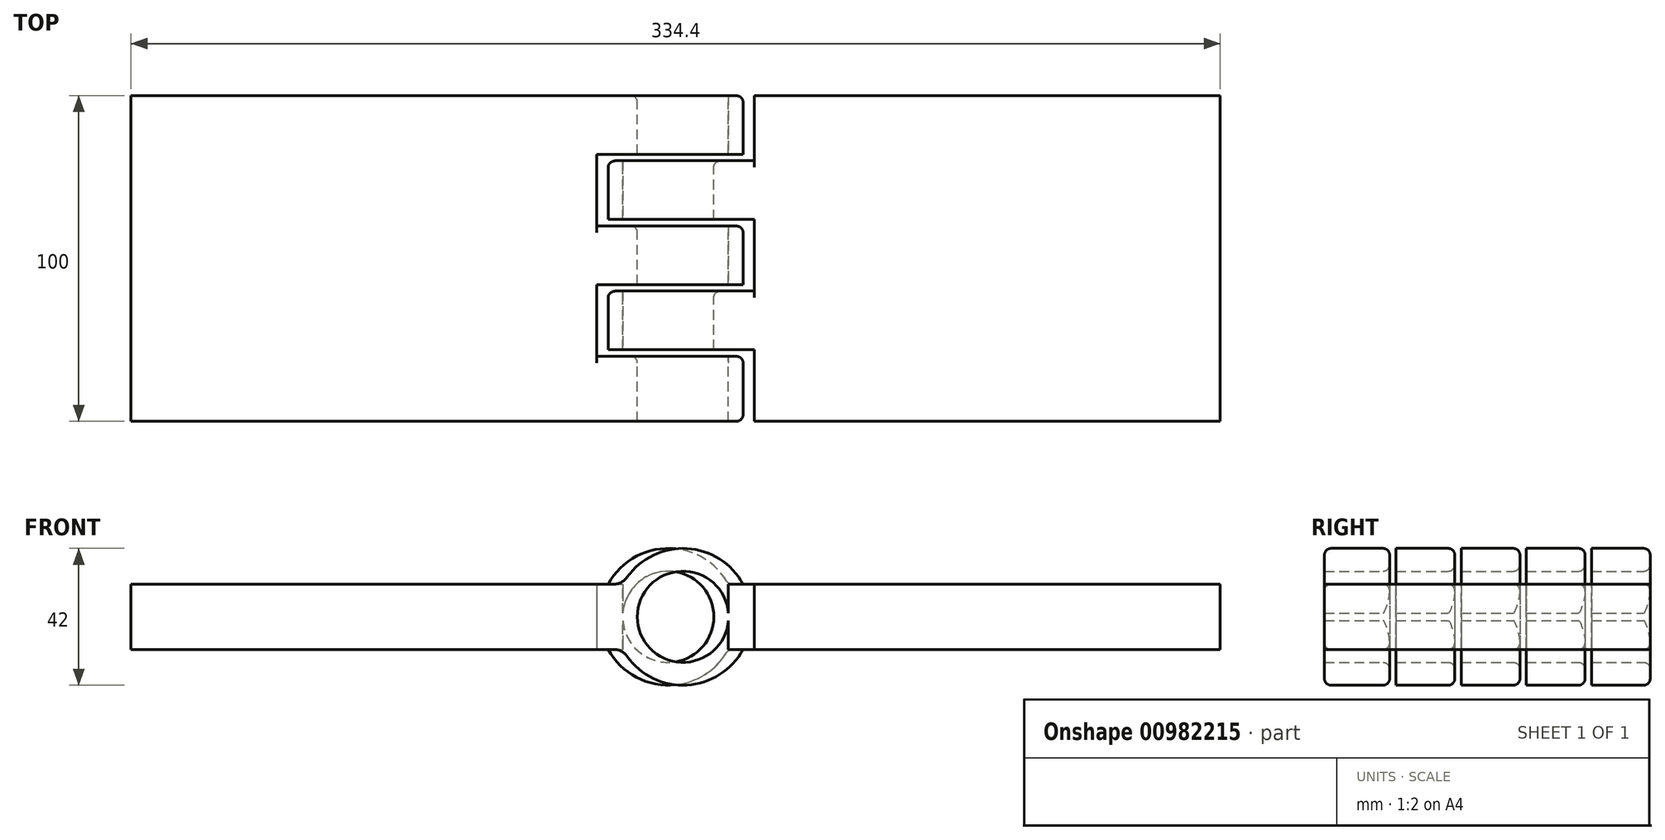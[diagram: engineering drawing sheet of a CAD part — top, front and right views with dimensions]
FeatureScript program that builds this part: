
annotation { "Feature Type Name" : "Feature", "Feature Type Description" : "" }
export const myFeature = defineFeature(function(context is Context, id is Id, definition is map)
    precondition{}
    {
        {
            var Q0;
            Q0=qCreatedBy(makeId("Front.planeOp"),FACE);
            var sketch = newSketch(context, id + "F0", { "sketchPlane" : qUnion([Q0])});
            skPoint(sketch, "E0.middle", {"position": v(0, 0) * mm});
            skPoint(sketch, "E0.left.start.orphan", {"position": v(100.03, 12.5) * mm});
            skPoint(sketch, "E1.orphan", {"position": v(100.2, -10) * mm});
            skArc(sketch, "E2", {"start": v(58.29, -10) * mm, "mid": v(97.76, 0) * mm, "end": v(58.29, 10) * mm});
            skCircle(sketch, "E3", {"center": v(76.76, 0) * mm, "radius": 10 * mm});
            skLineSegment(sketch, "E4", {"start": v(-92.7, 10) * mm, "end": v(77.7, 10) * mm});
            skLineSegment(sketch, "E5", {"start": v(-92.7, -10) * mm, "end": v(103.14, -10) * mm});
            skLineSegment(sketch, "E6", {"start": v(-92.7, 10) * mm, "end": v(-92.7, -10) * mm});
            skSolve(sketch);
        }
        {
            var Q0;
            Q0 = qSketchRegion(id + "F0", true);
            extrude(context, id + "F1", {"entities" : qUnion([Q0]), "oppositeDirection" : true, "depth" : 50 * mm, "offsetDistance" : 25 * mm, "hasSecondDirection" : true, "secondDirectionOppositeDirection" : false, "secondDirectionDepth" : 50 * mm});
        }
        {
            var Q0;
            Q0=makeQuery(id+"F1.opExtrude","CAP_FACE",FACE,{"disambiguationData":[OSD([sQuery(id+"F0.wireOp",EDGE,"DXCdCOsZ-PZph-URoq-5IPF-RWo1TbqNF6ah"),sQuery(id+"F0.wireOp",EDGE,"ewKAHVJC-rmJ0-RbaL-eWMY-Gv7xBNoriCzo"),sQuery(id+"F0.wireOp",EDGE,"E2"),sQuery(id+"F0.wireOp",EDGE,"d9418fdb-b965-4b45-a9c3-fe8144ecca6f.trimOffspring")])],"isStart":true});
            var sketch = newSketch(context, id + "F2", { "sketchPlane" : qUnion([Q0])});
            skCircle(sketch, "E7", {"center": v(76.76, 0) * mm, "radius": 14 * mm});
            skSolve(sketch);
        }
        {
            var Q0;
            Q0=makeQuery(id+"F2.imprint","IMPRINT",FACE,{"disambiguationData":[TD([[makeQuery(id+"F2.imprint","IMPRINT",EDGE,{"derivedFrom":sQuery(id+"F2.wireOp",EDGE,"E7")}),1.0]])]});
            extrude(context, id + "F3", {"entities" : qUnion([Q0]), "operationType" : NewBodyOperationType.REMOVE, "depth" : 25 * mm, "offsetDistance" : 25 * mm, "hasSecondDirection" : true, "secondDirectionOppositeDirection" : true, "secondDirectionDepth" : 160.8 * mm});
        }
        {
            var Q0;
            Q0=qCreatedBy(makeId("Right.planeOp"),FACE);
            cPlane(context, id + "F4", {"entities" : qUnion([Q0]), "cplaneType" : CPlaneType.OFFSET, "offset" : 100 * mm, "width" : 150 * mm, "height" : 150 * mm});
        }
        {
            var Q0;
            Q0=makeQuery(id+"F1.opExtrude","SWEPT_BODY",BODY,{"disambiguationData":[OSD([sQuery(id+"F0.wireOp",EDGE,"DXCdCOsZ-PZph-URoq-5IPF-RWo1TbqNF6ah"),sQuery(id+"F0.wireOp",EDGE,"ewKAHVJC-rmJ0-RbaL-eWMY-Gv7xBNoriCzo"),sQuery(id+"F0.wireOp",EDGE,"E2"),sQuery(id+"F0.wireOp",EDGE,"d9418fdb-b965-4b45-a9c3-fe8144ecca6f.trimOffspring")])]});
            var Q1;
            Q1=qCreatedBy(id+"F4.planeOp",FACE);
            mirror(context, id + "F5", {"entities" : qUnion([Q0]), "mirrorPlane" : qUnion([Q1])});
        }
        {
            var Q0;
            Q0=qCreatedBy(makeId("Top.planeOp"),FACE);
            var sketch = newSketch(context, id + "F6", { "sketchPlane" : qUnion([Q0])});
            skLineSegment(sketch, "E8.bottom", {"start": v(141.71, -50) * mm, "end": v(58.29, -50) * mm});
            skLineSegment(sketch, "E8.top", {"start": v(141.71, 50) * mm, "end": v(58.29, 50) * mm});
            skLineSegment(sketch, "E8.left", {"start": v(141.71, -50) * mm, "end": v(141.71, 50) * mm});
            skLineSegment(sketch, "E8.right", {"start": v(58.29, -50) * mm, "end": v(58.29, 50) * mm});
            skPoint(sketch, "E8.middle", {"position": v(100, 0) * mm});
            skLineSegment(sketch, "E9", {"start": v(58.29, 30) * mm, "end": v(141.71, 30) * mm});
            skLineSegment(sketch, "E10", {"start": v(58.29, -10) * mm, "end": v(141.71, -10) * mm});
            skLineSegment(sketch, "E11", {"start": v(141.71, -30) * mm, "end": v(58.29, -30) * mm});
            skLineSegment(sketch, "E12", {"start": v(141.71, 10) * mm, "end": v(58.29, 10) * mm});
            skLineSegment(sketch, "E13", {"start": v(100.25, 50) * mm, "end": v(100.25, -50) * mm});
            skSolve(sketch);
        }
        {
            var Q0;
            {var subQ0=sQuery(id+"F6.wireOp",EDGE,"E9");var subQ1=sQuery(id+"F6.wireOp",EDGE,"E8.right");var subQ2=makeQuery(id+"F6.imprint","INTERSECT",VERTEX,{"derivedFrom":[subQ1,subQ0]});Q0=makeQuery(id+"F6.imprint","IMPRINT",FACE,{"disambiguationData":[TD([[makeQuery(id+"F6.imprint","IMPRINT",EDGE,{"disambiguationData":[TD([[subQ2,1.0]])],"derivedFrom":subQ1}),-1.0]])]});}
            var Q1;
            {var subQ0=sQuery(id+"F6.wireOp",EDGE,"E10");var subQ1=sQuery(id+"F6.wireOp",EDGE,"E8.right");var subQ2=makeQuery(id+"F6.imprint","INTERSECT",VERTEX,{"derivedFrom":[subQ1,subQ0]});Q1=makeQuery(id+"F6.imprint","IMPRINT",FACE,{"disambiguationData":[TD([[makeQuery(id+"F6.imprint","IMPRINT",EDGE,{"disambiguationData":[TD([[subQ2,1.0]])],"derivedFrom":subQ1}),-1.0]])]});}
            extrude(context, id + "F7", {"entities" : qUnion([Q0, Q1]), "operationType" : NewBodyOperationType.REMOVE, "depth" : 25 * mm, "offsetDistance" : 25 * mm, "hasSecondDirection" : true, "secondDirectionOppositeDirection" : true, "secondDirectionDepth" : 25 * mm});
        }
        {
            var Q0;
            {var subQ0=sQuery(id+"F6.wireOp",EDGE,"E8.left");var subQ1=sQuery(id+"F6.wireOp",EDGE,"E8.top");var subQ2=makeQuery(id+"F6.imprint","INTERSECT",VERTEX,{"derivedFrom":[subQ1,subQ0]});Q0=makeQuery(id+"F6.imprint","IMPRINT",FACE,{"disambiguationData":[TD([[makeQuery(id+"F6.imprint","IMPRINT",EDGE,{"disambiguationData":[TD([[subQ2,-1.0]])],"derivedFrom":subQ1}),1.0]])]});}
            var Q1;
            {var subQ0=sQuery(id+"F6.wireOp",EDGE,"E8.left");var subQ1=sQuery(id+"F6.wireOp",EDGE,"E8.bottom");var subQ2=makeQuery(id+"F6.imprint","INTERSECT",VERTEX,{"derivedFrom":[subQ1,subQ0]});Q1=makeQuery(id+"F6.imprint","IMPRINT",FACE,{"disambiguationData":[TD([[makeQuery(id+"F6.imprint","IMPRINT",EDGE,{"disambiguationData":[TD([[subQ2,-1.0]])],"derivedFrom":subQ1}),-1.0]])]});}
            var Q2;
            {var subQ0=sQuery(id+"F6.wireOp",EDGE,"E10");var subQ1=sQuery(id+"F6.wireOp",EDGE,"E8.left");var subQ2=makeQuery(id+"F6.imprint","INTERSECT",VERTEX,{"derivedFrom":[subQ1,subQ0]});Q2=makeQuery(id+"F6.imprint","IMPRINT",FACE,{"disambiguationData":[TD([[makeQuery(id+"F6.imprint","IMPRINT",EDGE,{"disambiguationData":[TD([[subQ2,-1.0]])],"derivedFrom":subQ1}),1.0]])]});}
            extrude(context, id + "F8", {"entities" : qUnion([Q0, Q1, Q2]), "operationType" : NewBodyOperationType.REMOVE, "depth" : 32 * mm, "offsetDistance" : 25 * mm, "hasSecondDirection" : true, "secondDirectionOppositeDirection" : true, "secondDirectionDepth" : 48 * mm});
        }
        {
            var Q0;
            Q0=makeQuery(id+"F5.opPattern","COPY",BODY,{"derivedFrom":makeQuery(id+"F1.opExtrude","SWEPT_BODY",BODY,{"disambiguationData":[OSD([sQuery(id+"F0.wireOp",EDGE,"DXCdCOsZ-PZph-URoq-5IPF-RWo1TbqNF6ah"),sQuery(id+"F0.wireOp",EDGE,"ewKAHVJC-rmJ0-RbaL-eWMY-Gv7xBNoriCzo"),sQuery(id+"F0.wireOp",EDGE,"E2"),sQuery(id+"F0.wireOp",EDGE,"d9418fdb-b965-4b45-a9c3-fe8144ecca6f.trimOffspring")])]}),"instanceName":"1"});
            transform(context, id + "F9", {"entities" : qUnion([Q0]), "transformType" : TransformType.TRANSLATION_3D, "dx" : -51 * mm, "dy" : 0 * mm, "dz" : 0 * mm, "makeCopy" : false});
        }
        {
            var Q0;
            {var subQ0=sQuery(id+"F6.wireOp",EDGE,"E8.right");Q0=makeQuery(id+"F7.boolean.opBoolean","COPY",FACE,{"derivedFrom":makeQuery(id+"F7.opExtrude","SWEPT_FACE",FACE,{"disambiguationData":[OSD([subQ0]),TDD([makeQuery(id+"F6.imprint","IMPRINT",EDGE,{"disambiguationData":[TD([[makeQuery(id+"F6.imprint","INTERSECT",VERTEX,{"derivedFrom":[subQ0,sQuery(id+"F6.wireOp",EDGE,"E10")]}),1.0]])],"derivedFrom":subQ0})])]})});}
            var Q1;
            {var subQ0=sQuery(id+"F6.wireOp",EDGE,"E8.right");Q1=makeQuery(id+"F7.boolean.opBoolean","COPY",FACE,{"derivedFrom":makeQuery(id+"F7.opExtrude","SWEPT_FACE",FACE,{"disambiguationData":[OSD([subQ0]),TDD([makeQuery(id+"F6.imprint","IMPRINT",EDGE,{"disambiguationData":[TD([[makeQuery(id+"F6.imprint","INTERSECT",VERTEX,{"derivedFrom":[subQ0,sQuery(id+"F6.wireOp",EDGE,"E9")]}),1.0]])],"derivedFrom":subQ0})])]})});}
            extrude(context, id + "F10", {"entities" : qUnion([Q0, Q1]), "operationType" : NewBodyOperationType.REMOVE, "oppositeDirection" : true, "depth" : 8 * mm, "offsetDistance" : 25 * mm});
        }
        {
            var Q0;
            {var subQ0=sQuery(id+"F6.wireOp",EDGE,"E8.left");Q0=makeQuery(id+"F8.boolean.opBoolean","COPY",FACE,{"derivedFrom":makeQuery(id+"F8.opExtrude","SWEPT_FACE",FACE,{"disambiguationData":[OSD([subQ0]),TDD([makeQuery(id+"F6.imprint","IMPRINT",EDGE,{"disambiguationData":[TD([[makeQuery(id+"F6.imprint","INTERSECT",VERTEX,{"derivedFrom":[sQuery(id+"F6.wireOp",EDGE,"E8.top"),subQ0]}),1.0]])],"derivedFrom":subQ0})])]})});}
            var Q1;
            {var subQ0=sQuery(id+"F6.wireOp",EDGE,"E8.left");Q1=makeQuery(id+"F8.boolean.opBoolean","COPY",FACE,{"derivedFrom":makeQuery(id+"F8.opExtrude","SWEPT_FACE",FACE,{"disambiguationData":[OSD([subQ0]),TDD([makeQuery(id+"F6.imprint","IMPRINT",EDGE,{"disambiguationData":[TD([[makeQuery(id+"F6.imprint","INTERSECT",VERTEX,{"derivedFrom":[subQ0,sQuery(id+"F6.wireOp",EDGE,"E10")]}),-1.0]])],"derivedFrom":subQ0})])]})});}
            var Q2;
            {var subQ0=sQuery(id+"F6.wireOp",EDGE,"E8.left");Q2=makeQuery(id+"F8.boolean.opBoolean","COPY",FACE,{"derivedFrom":makeQuery(id+"F8.opExtrude","SWEPT_FACE",FACE,{"disambiguationData":[OSD([subQ0]),TDD([makeQuery(id+"F6.imprint","IMPRINT",EDGE,{"disambiguationData":[TD([[makeQuery(id+"F6.imprint","INTERSECT",VERTEX,{"derivedFrom":[sQuery(id+"F6.wireOp",EDGE,"E8.bottom"),subQ0]}),-1.0]])],"derivedFrom":subQ0})])]})});}
            extrude(context, id + "F11", {"entities" : qUnion([Q0, Q1, Q2]), "operationType" : NewBodyOperationType.REMOVE, "oppositeDirection" : true, "depth" : 8 * mm, "offsetDistance" : 25 * mm});
        }
        {
            var Q0;
            {var subQ0=sQuery(id+"F6.wireOp",EDGE,"E9");Q0=makeQuery(id+"F10.boolean.opBoolean","MERGE",FACE,{"derivedFrom":[makeQuery(id+"F7.boolean.opBoolean","COPY",FACE,{"derivedFrom":makeQuery(id+"F7.opExtrude","SWEPT_FACE",FACE,{"disambiguationData":[OSD([subQ0])]})})],"fromTools":[makeQuery(id+"F10.opExtrude","SWEPT_FACE",FACE,{"disambiguationData":[OSD([sQuery(id+"F6.wireOp",EDGE,"E8.right"),subQ0])]})]});}
            var Q1;
            {var subQ0=sQuery(id+"F6.wireOp",EDGE,"E10");Q1=makeQuery(id+"F10.boolean.opBoolean","MERGE",FACE,{"derivedFrom":[makeQuery(id+"F7.boolean.opBoolean","COPY",FACE,{"derivedFrom":makeQuery(id+"F7.opExtrude","SWEPT_FACE",FACE,{"disambiguationData":[OSD([subQ0])]})})],"fromTools":[makeQuery(id+"F10.opExtrude","SWEPT_FACE",FACE,{"disambiguationData":[OSD([sQuery(id+"F6.wireOp",EDGE,"E8.right"),subQ0])]})]});}
            var Q2;
            {var subQ0=sQuery(id+"F6.wireOp",EDGE,"E11");Q2=makeQuery(id+"F10.boolean.opBoolean","MERGE",FACE,{"derivedFrom":[makeQuery(id+"F7.boolean.opBoolean","COPY",FACE,{"derivedFrom":makeQuery(id+"F7.opExtrude","SWEPT_FACE",FACE,{"disambiguationData":[OSD([subQ0])]})})],"fromTools":[makeQuery(id+"F10.opExtrude","SWEPT_FACE",FACE,{"disambiguationData":[OSD([sQuery(id+"F6.wireOp",EDGE,"E8.right"),subQ0])]})]});}
            var Q3;
            {var subQ0=sQuery(id+"F6.wireOp",EDGE,"E12");Q3=makeQuery(id+"F10.boolean.opBoolean","MERGE",FACE,{"derivedFrom":[makeQuery(id+"F7.boolean.opBoolean","COPY",FACE,{"derivedFrom":makeQuery(id+"F7.opExtrude","SWEPT_FACE",FACE,{"disambiguationData":[OSD([subQ0])]})})],"fromTools":[makeQuery(id+"F10.opExtrude","SWEPT_FACE",FACE,{"disambiguationData":[OSD([sQuery(id+"F6.wireOp",EDGE,"E8.right"),subQ0])]})]});}
            extrude(context, id + "F12", {"entities" : qUnion([Q0, Q1, Q2, Q3]), "operationType" : NewBodyOperationType.REMOVE, "oppositeDirection" : true, "depth" : 2 * mm, "offsetDistance" : 25 * mm});
        }
        {
            var Q0;
            {var subQ0=sQuery(id+"F6.wireOp",EDGE,"E11");Q0=makeQuery(id+"F11.boolean.opBoolean","MERGE",FACE,{"derivedFrom":[makeQuery(id+"F8.boolean.opBoolean","COPY",FACE,{"derivedFrom":makeQuery(id+"F8.opExtrude","SWEPT_FACE",FACE,{"disambiguationData":[OSD([subQ0])]})})],"fromTools":[makeQuery(id+"F11.opExtrude","SWEPT_FACE",FACE,{"disambiguationData":[OSD([sQuery(id+"F6.wireOp",EDGE,"E8.left"),subQ0])]})]});}
            var Q1;
            {var subQ0=sQuery(id+"F6.wireOp",EDGE,"E12");Q1=makeQuery(id+"F11.boolean.opBoolean","MERGE",FACE,{"derivedFrom":[makeQuery(id+"F8.boolean.opBoolean","COPY",FACE,{"derivedFrom":makeQuery(id+"F8.opExtrude","SWEPT_FACE",FACE,{"disambiguationData":[OSD([subQ0])]})})],"fromTools":[makeQuery(id+"F11.opExtrude","SWEPT_FACE",FACE,{"disambiguationData":[OSD([sQuery(id+"F6.wireOp",EDGE,"E8.left"),subQ0])]})]});}
            var Q2;
            {var subQ0=sQuery(id+"F6.wireOp",EDGE,"E10");Q2=makeQuery(id+"F11.boolean.opBoolean","MERGE",FACE,{"derivedFrom":[makeQuery(id+"F8.boolean.opBoolean","COPY",FACE,{"derivedFrom":makeQuery(id+"F8.opExtrude","SWEPT_FACE",FACE,{"disambiguationData":[OSD([subQ0])]})})],"fromTools":[makeQuery(id+"F11.opExtrude","SWEPT_FACE",FACE,{"disambiguationData":[OSD([sQuery(id+"F6.wireOp",EDGE,"E8.left"),subQ0])]})]});}
            var Q3;
            {var subQ0=sQuery(id+"F6.wireOp",EDGE,"E9");Q3=makeQuery(id+"F11.boolean.opBoolean","MERGE",FACE,{"derivedFrom":[makeQuery(id+"F8.boolean.opBoolean","COPY",FACE,{"derivedFrom":makeQuery(id+"F8.opExtrude","SWEPT_FACE",FACE,{"disambiguationData":[OSD([subQ0])]})})],"fromTools":[makeQuery(id+"F11.opExtrude","SWEPT_FACE",FACE,{"disambiguationData":[OSD([sQuery(id+"F6.wireOp",EDGE,"E8.left"),subQ0])]})]});}
            extrude(context, id + "F13", {"entities" : qUnion([Q0, Q1, Q2, Q3]), "operationType" : NewBodyOperationType.REMOVE, "oppositeDirection" : true, "depth" : 2 * mm, "offsetDistance" : 25 * mm});
        }
        {
            var Q0;
            {var subQ0=sQuery(id+"F0.wireOp",EDGE,"d9418fdb-b965-4b45-a9c3-fe8144ecca6f.trimOffspring");var subQ1=sQuery(id+"F6.wireOp",EDGE,"E8.left");var subQ2=sQuery(id+"F0.wireOp",EDGE,"E2");Q0=makeQuery(id+"F11.boolean.opBoolean","COPY",EDGE,{"derivedFrom":makeQuery(id+"F11.opExtrude","CAP_EDGE",EDGE,{"disambiguationData":[OSD([subQ2,subQ0]),TDD([makeQuery(id+"F8.boolean.opBoolean","SPLIT",EDGE,{"disambiguationData":[topologyDisambiguationEdgeConnected([makeQuery(id+"F5.opPattern","COPY",FACE,{"derivedFrom":makeQuery(id+"F1.opExtrude","SWEPT_FACE",FACE,{"disambiguationData":[OSD([subQ0])]}),"instanceName":"1"}),makeQuery(id+"F8.opExtrude","SWEPT_FACE",FACE,{"disambiguationData":[OSD([subQ1]),TDD([makeQuery(id+"F6.imprint","IMPRINT",EDGE,{"disambiguationData":[TD([[makeQuery(id+"F6.imprint","INTERSECT",VERTEX,{"derivedFrom":[sQuery(id+"F6.wireOp",EDGE,"E8.top"),subQ1]}),1.0]])],"derivedFrom":subQ1})])]})])],"derivedFrom":makeQuery(id+"F5.opPattern","COPY",EDGE,{"derivedFrom":makeQuery(id+"F1.opExtrude","SWEPT_EDGE",EDGE,{"disambiguationData":[OSD([subQ2,subQ0])]}),"instanceName":"1"})})])],"isStart":false})});}
            var Q1;
            {var subQ0=sQuery(id+"F6.wireOp",EDGE,"E12");var subQ1=sQuery(id+"F0.wireOp",EDGE,"E2");var subQ2=sQuery(id+"F0.wireOp",EDGE,"d9418fdb-b965-4b45-a9c3-fe8144ecca6f.trimOffspring");var subQ3=sQuery(id+"F6.wireOp",EDGE,"E8.left");Q1=makeQuery(id+"F13.boolean.opBoolean","MERGE",EDGE,{"derivedFrom":[makeQuery(id+"F11.boolean.opBoolean","COPY",EDGE,{"derivedFrom":makeQuery(id+"F11.opExtrude","CAP_EDGE",EDGE,{"disambiguationData":[OSD([subQ1,subQ2]),TDD([makeQuery(id+"F8.boolean.opBoolean","SPLIT",EDGE,{"disambiguationData":[topologyDisambiguationEdgeConnected([makeQuery(id+"F5.opPattern","COPY",FACE,{"derivedFrom":makeQuery(id+"F1.opExtrude","SWEPT_FACE",FACE,{"disambiguationData":[OSD([subQ2])]}),"instanceName":"1"}),makeQuery(id+"F8.opExtrude","SWEPT_FACE",FACE,{"disambiguationData":[OSD([subQ3]),TDD([makeQuery(id+"F6.imprint","IMPRINT",EDGE,{"disambiguationData":[TD([[makeQuery(id+"F6.imprint","INTERSECT",VERTEX,{"derivedFrom":[subQ3,sQuery(id+"F6.wireOp",EDGE,"E10")]}),-1.0]])],"derivedFrom":subQ3})])]})])],"derivedFrom":makeQuery(id+"F5.opPattern","COPY",EDGE,{"derivedFrom":makeQuery(id+"F1.opExtrude","SWEPT_EDGE",EDGE,{"disambiguationData":[OSD([subQ1,subQ2])]}),"instanceName":"1"})})])],"isStart":false})})],"fromTools":[makeQuery(id+"F13.opExtrude","SWEPT_EDGE",EDGE,{"disambiguationData":[OSD([subQ1,subQ0]),TDD([makeQuery(id+"F11.boolean.opBoolean","COPY",VERTEX,{"derivedFrom":makeQuery(id+"F11.opExtrude","CAP_VERTEX",VERTEX,{"disambiguationData":[OSD([subQ1,subQ0]),TDD([makeQuery(id+"F8.boolean.opBoolean","INTERSECT",VERTEX,{"disambiguationData":[OD(1.0)],"derivedFrom":[makeQuery(id+"F5.opPattern","COPY",FACE,{"derivedFrom":makeQuery(id+"F1.opExtrude","SWEPT_FACE",FACE,{"disambiguationData":[OSD([subQ1])]}),"instanceName":"1"}),makeQuery(id+"F8.opExtrude","SWEPT_FACE",FACE,{"disambiguationData":[OSD([subQ0])]})]})])],"isStart":false})})])]})]});}
            var Q2;
            {var subQ0=sQuery(id+"F6.wireOp",EDGE,"E11");var subQ1=sQuery(id+"F0.wireOp",EDGE,"E2");var subQ2=sQuery(id+"F0.wireOp",EDGE,"d9418fdb-b965-4b45-a9c3-fe8144ecca6f.trimOffspring");var subQ3=sQuery(id+"F6.wireOp",EDGE,"E8.left");Q2=makeQuery(id+"F13.boolean.opBoolean","MERGE",EDGE,{"derivedFrom":[makeQuery(id+"F11.boolean.opBoolean","COPY",EDGE,{"derivedFrom":makeQuery(id+"F11.opExtrude","CAP_EDGE",EDGE,{"disambiguationData":[OSD([subQ1,subQ2]),TDD([makeQuery(id+"F8.boolean.opBoolean","SPLIT",EDGE,{"disambiguationData":[topologyDisambiguationEdgeConnected([makeQuery(id+"F5.opPattern","COPY",FACE,{"derivedFrom":makeQuery(id+"F1.opExtrude","SWEPT_FACE",FACE,{"disambiguationData":[OSD([subQ2])]}),"instanceName":"1"}),makeQuery(id+"F8.opExtrude","SWEPT_FACE",FACE,{"disambiguationData":[OSD([subQ3]),TDD([makeQuery(id+"F6.imprint","IMPRINT",EDGE,{"disambiguationData":[TD([[makeQuery(id+"F6.imprint","INTERSECT",VERTEX,{"derivedFrom":[sQuery(id+"F6.wireOp",EDGE,"E8.bottom"),subQ3]}),-1.0]])],"derivedFrom":subQ3})])]})])],"derivedFrom":makeQuery(id+"F5.opPattern","COPY",EDGE,{"derivedFrom":makeQuery(id+"F1.opExtrude","SWEPT_EDGE",EDGE,{"disambiguationData":[OSD([subQ1,subQ2])]}),"instanceName":"1"})})])],"isStart":false})})],"fromTools":[makeQuery(id+"F13.opExtrude","SWEPT_EDGE",EDGE,{"disambiguationData":[OSD([subQ1,subQ0]),TDD([makeQuery(id+"F11.boolean.opBoolean","COPY",VERTEX,{"derivedFrom":makeQuery(id+"F11.opExtrude","CAP_VERTEX",VERTEX,{"disambiguationData":[OSD([subQ1,subQ0]),TDD([makeQuery(id+"F8.boolean.opBoolean","INTERSECT",VERTEX,{"disambiguationData":[OD(1.0)],"derivedFrom":[makeQuery(id+"F5.opPattern","COPY",FACE,{"derivedFrom":makeQuery(id+"F1.opExtrude","SWEPT_FACE",FACE,{"disambiguationData":[OSD([subQ1])]}),"instanceName":"1"}),makeQuery(id+"F8.opExtrude","SWEPT_FACE",FACE,{"disambiguationData":[OSD([subQ0])]})]})])],"isStart":false})})])]})]});}
            var Q3;
            {var subQ0=sQuery(id+"F6.wireOp",EDGE,"E10");var subQ1=sQuery(id+"F0.wireOp",EDGE,"E2");var subQ2=sQuery(id+"F0.wireOp",EDGE,"d9418fdb-b965-4b45-a9c3-fe8144ecca6f.trimOffspring");var subQ3=sQuery(id+"F6.wireOp",EDGE,"E8.right");Q3=makeQuery(id+"F12.boolean.opBoolean","MERGE",EDGE,{"derivedFrom":[makeQuery(id+"F10.boolean.opBoolean","COPY",EDGE,{"derivedFrom":makeQuery(id+"F10.opExtrude","CAP_EDGE",EDGE,{"disambiguationData":[OSD([subQ1,subQ2]),TDD([makeQuery(id+"F7.boolean.opBoolean","SPLIT",EDGE,{"disambiguationData":[topologyDisambiguationEdgeConnected([makeQuery(id+"F1.opExtrude","SWEPT_FACE",FACE,{"disambiguationData":[OSD([subQ2])]}),makeQuery(id+"F7.opExtrude","SWEPT_FACE",FACE,{"disambiguationData":[OSD([subQ3]),TDD([makeQuery(id+"F6.imprint","IMPRINT",EDGE,{"disambiguationData":[TD([[makeQuery(id+"F6.imprint","INTERSECT",VERTEX,{"derivedFrom":[subQ3,subQ0]}),1.0]])],"derivedFrom":subQ3})])]})])],"derivedFrom":makeQuery(id+"F1.opExtrude","SWEPT_EDGE",EDGE,{"disambiguationData":[OSD([subQ1,subQ2])]})})])],"isStart":false})})],"fromTools":[makeQuery(id+"F12.opExtrude","SWEPT_EDGE",EDGE,{"disambiguationData":[OSD([subQ1,subQ0]),TDD([makeQuery(id+"F10.boolean.opBoolean","COPY",VERTEX,{"derivedFrom":makeQuery(id+"F10.opExtrude","CAP_VERTEX",VERTEX,{"disambiguationData":[OSD([subQ1,subQ0]),TDD([makeQuery(id+"F7.boolean.opBoolean","INTERSECT",VERTEX,{"disambiguationData":[OD(1.0)],"derivedFrom":[makeQuery(id+"F1.opExtrude","SWEPT_FACE",FACE,{"disambiguationData":[OSD([subQ1])]}),makeQuery(id+"F7.opExtrude","SWEPT_FACE",FACE,{"disambiguationData":[OSD([subQ0])]})]})])],"isStart":false})})])]})]});}
            var Q4;
            {var subQ0=sQuery(id+"F6.wireOp",EDGE,"E9");var subQ1=sQuery(id+"F0.wireOp",EDGE,"E2");var subQ2=sQuery(id+"F0.wireOp",EDGE,"d9418fdb-b965-4b45-a9c3-fe8144ecca6f.trimOffspring");var subQ3=sQuery(id+"F6.wireOp",EDGE,"E8.right");Q4=makeQuery(id+"F12.boolean.opBoolean","MERGE",EDGE,{"derivedFrom":[makeQuery(id+"F10.boolean.opBoolean","COPY",EDGE,{"derivedFrom":makeQuery(id+"F10.opExtrude","CAP_EDGE",EDGE,{"disambiguationData":[OSD([subQ1,subQ2]),TDD([makeQuery(id+"F7.boolean.opBoolean","SPLIT",EDGE,{"disambiguationData":[topologyDisambiguationEdgeConnected([makeQuery(id+"F1.opExtrude","SWEPT_FACE",FACE,{"disambiguationData":[OSD([subQ2])]}),makeQuery(id+"F7.opExtrude","SWEPT_FACE",FACE,{"disambiguationData":[OSD([subQ3]),TDD([makeQuery(id+"F6.imprint","IMPRINT",EDGE,{"disambiguationData":[TD([[makeQuery(id+"F6.imprint","INTERSECT",VERTEX,{"derivedFrom":[subQ3,subQ0]}),1.0]])],"derivedFrom":subQ3})])]})])],"derivedFrom":makeQuery(id+"F1.opExtrude","SWEPT_EDGE",EDGE,{"disambiguationData":[OSD([subQ1,subQ2])]})})])],"isStart":false})})],"fromTools":[makeQuery(id+"F12.opExtrude","SWEPT_EDGE",EDGE,{"disambiguationData":[OSD([subQ1,subQ0]),TDD([makeQuery(id+"F10.boolean.opBoolean","COPY",VERTEX,{"derivedFrom":makeQuery(id+"F10.opExtrude","CAP_VERTEX",VERTEX,{"disambiguationData":[OSD([subQ1,subQ0]),TDD([makeQuery(id+"F7.boolean.opBoolean","INTERSECT",VERTEX,{"disambiguationData":[OD(1.0)],"derivedFrom":[makeQuery(id+"F1.opExtrude","SWEPT_FACE",FACE,{"disambiguationData":[OSD([subQ1])]}),makeQuery(id+"F7.opExtrude","SWEPT_FACE",FACE,{"disambiguationData":[OSD([subQ0])]})]})])],"isStart":false})})])]})]});}
            var Q5;
            {var subQ0=sQuery(id+"F6.wireOp",EDGE,"E10");var subQ1=sQuery(id+"F0.wireOp",EDGE,"E2");var subQ2=sQuery(id+"F0.wireOp",EDGE,"DXCdCOsZ-PZph-URoq-5IPF-RWo1TbqNF6ah");var subQ3=sQuery(id+"F6.wireOp",EDGE,"E8.right");Q5=makeQuery(id+"F12.boolean.opBoolean","MERGE",EDGE,{"derivedFrom":[makeQuery(id+"F10.boolean.opBoolean","COPY",EDGE,{"derivedFrom":makeQuery(id+"F10.opExtrude","CAP_EDGE",EDGE,{"disambiguationData":[OSD([subQ2,subQ1]),TDD([makeQuery(id+"F7.boolean.opBoolean","SPLIT",EDGE,{"disambiguationData":[topologyDisambiguationEdgeConnected([makeQuery(id+"F1.opExtrude","SWEPT_FACE",FACE,{"disambiguationData":[OSD([subQ2])]}),makeQuery(id+"F7.opExtrude","SWEPT_FACE",FACE,{"disambiguationData":[OSD([subQ3]),TDD([makeQuery(id+"F6.imprint","IMPRINT",EDGE,{"disambiguationData":[TD([[makeQuery(id+"F6.imprint","INTERSECT",VERTEX,{"derivedFrom":[subQ3,subQ0]}),1.0]])],"derivedFrom":subQ3})])]})])],"derivedFrom":makeQuery(id+"F1.opExtrude","SWEPT_EDGE",EDGE,{"disambiguationData":[OSD([subQ2,subQ1])]})})])],"isStart":false})})],"fromTools":[makeQuery(id+"F12.opExtrude","SWEPT_EDGE",EDGE,{"disambiguationData":[OSD([subQ1,subQ0]),TDD([makeQuery(id+"F10.boolean.opBoolean","COPY",VERTEX,{"derivedFrom":makeQuery(id+"F10.opExtrude","CAP_VERTEX",VERTEX,{"disambiguationData":[OSD([subQ1,subQ0]),TDD([makeQuery(id+"F7.boolean.opBoolean","INTERSECT",VERTEX,{"disambiguationData":[OD(0.0)],"derivedFrom":[makeQuery(id+"F1.opExtrude","SWEPT_FACE",FACE,{"disambiguationData":[OSD([subQ1])]}),makeQuery(id+"F7.opExtrude","SWEPT_FACE",FACE,{"disambiguationData":[OSD([subQ0])]})]})])],"isStart":false})})])]})]});}
            var Q6;
            {var subQ0=sQuery(id+"F6.wireOp",EDGE,"E12");var subQ1=sQuery(id+"F0.wireOp",EDGE,"E2");var subQ2=sQuery(id+"F0.wireOp",EDGE,"DXCdCOsZ-PZph-URoq-5IPF-RWo1TbqNF6ah");var subQ3=sQuery(id+"F6.wireOp",EDGE,"E8.left");Q6=makeQuery(id+"F13.boolean.opBoolean","MERGE",EDGE,{"derivedFrom":[makeQuery(id+"F11.boolean.opBoolean","COPY",EDGE,{"derivedFrom":makeQuery(id+"F11.opExtrude","CAP_EDGE",EDGE,{"disambiguationData":[OSD([subQ2,subQ1]),TDD([makeQuery(id+"F8.boolean.opBoolean","SPLIT",EDGE,{"disambiguationData":[topologyDisambiguationEdgeConnected([makeQuery(id+"F5.opPattern","COPY",FACE,{"derivedFrom":makeQuery(id+"F1.opExtrude","SWEPT_FACE",FACE,{"disambiguationData":[OSD([subQ2])]}),"instanceName":"1"}),makeQuery(id+"F8.opExtrude","SWEPT_FACE",FACE,{"disambiguationData":[OSD([subQ3]),TDD([makeQuery(id+"F6.imprint","IMPRINT",EDGE,{"disambiguationData":[TD([[makeQuery(id+"F6.imprint","INTERSECT",VERTEX,{"derivedFrom":[subQ3,sQuery(id+"F6.wireOp",EDGE,"E10")]}),-1.0]])],"derivedFrom":subQ3})])]})])],"derivedFrom":makeQuery(id+"F5.opPattern","COPY",EDGE,{"derivedFrom":makeQuery(id+"F1.opExtrude","SWEPT_EDGE",EDGE,{"disambiguationData":[OSD([subQ2,subQ1])]}),"instanceName":"1"})})])],"isStart":false})})],"fromTools":[makeQuery(id+"F13.opExtrude","SWEPT_EDGE",EDGE,{"disambiguationData":[OSD([subQ1,subQ0]),TDD([makeQuery(id+"F11.boolean.opBoolean","COPY",VERTEX,{"derivedFrom":makeQuery(id+"F11.opExtrude","CAP_VERTEX",VERTEX,{"disambiguationData":[OSD([subQ1,subQ0]),TDD([makeQuery(id+"F8.boolean.opBoolean","INTERSECT",VERTEX,{"disambiguationData":[OD(0.0)],"derivedFrom":[makeQuery(id+"F5.opPattern","COPY",FACE,{"derivedFrom":makeQuery(id+"F1.opExtrude","SWEPT_FACE",FACE,{"disambiguationData":[OSD([subQ1])]}),"instanceName":"1"}),makeQuery(id+"F8.opExtrude","SWEPT_FACE",FACE,{"disambiguationData":[OSD([subQ0])]})]})])],"isStart":false})})])]})]});}
            var Q7;
            {var subQ0=sQuery(id+"F6.wireOp",EDGE,"E9");var subQ2=sQuery(id+"F0.wireOp",EDGE,"E2");var subQ3=makeQuery(id+"F1.opExtrude","SWEPT_FACE",FACE,{"disambiguationData":[OSD([subQ2])]});var subQ4=sQuery(id+"F0.wireOp",EDGE,"DXCdCOsZ-PZph-URoq-5IPF-RWo1TbqNF6ah");var subQ5=makeQuery(id+"F1.opExtrude","SWEPT_FACE",FACE,{"disambiguationData":[OSD([subQ4])]});Q7=makeQuery(id+"F7.boolean.opBoolean","SPLIT",EDGE,{"disambiguationData":[topologyDisambiguationEdgeConnected([subQ5,subQ3]),TD([makeQuery(id+"F7.opExtrude","SWEPT_FACE",FACE,{"disambiguationData":[OSD([subQ0])]})])],"derivedFrom":makeQuery(id+"F1.opExtrude","SWEPT_EDGE",EDGE,{"disambiguationData":[OSD([subQ4,subQ2])]})});}
            var Q8;
            {var subQ0=sQuery(id+"F6.wireOp",EDGE,"E9");var subQ1=sQuery(id+"F0.wireOp",EDGE,"E2");var subQ2=sQuery(id+"F0.wireOp",EDGE,"DXCdCOsZ-PZph-URoq-5IPF-RWo1TbqNF6ah");var subQ3=sQuery(id+"F6.wireOp",EDGE,"E8.right");Q8=makeQuery(id+"F12.boolean.opBoolean","MERGE",EDGE,{"derivedFrom":[makeQuery(id+"F10.boolean.opBoolean","COPY",EDGE,{"derivedFrom":makeQuery(id+"F10.opExtrude","CAP_EDGE",EDGE,{"disambiguationData":[OSD([subQ2,subQ1]),TDD([makeQuery(id+"F7.boolean.opBoolean","SPLIT",EDGE,{"disambiguationData":[topologyDisambiguationEdgeConnected([makeQuery(id+"F1.opExtrude","SWEPT_FACE",FACE,{"disambiguationData":[OSD([subQ2])]}),makeQuery(id+"F7.opExtrude","SWEPT_FACE",FACE,{"disambiguationData":[OSD([subQ3]),TDD([makeQuery(id+"F6.imprint","IMPRINT",EDGE,{"disambiguationData":[TD([[makeQuery(id+"F6.imprint","INTERSECT",VERTEX,{"derivedFrom":[subQ3,subQ0]}),1.0]])],"derivedFrom":subQ3})])]})])],"derivedFrom":makeQuery(id+"F1.opExtrude","SWEPT_EDGE",EDGE,{"disambiguationData":[OSD([subQ2,subQ1])]})})])],"isStart":false})})],"fromTools":[makeQuery(id+"F12.opExtrude","SWEPT_EDGE",EDGE,{"disambiguationData":[OSD([subQ1,subQ0]),TDD([makeQuery(id+"F10.boolean.opBoolean","COPY",VERTEX,{"derivedFrom":makeQuery(id+"F10.opExtrude","CAP_VERTEX",VERTEX,{"disambiguationData":[OSD([subQ1,subQ0]),TDD([makeQuery(id+"F7.boolean.opBoolean","INTERSECT",VERTEX,{"disambiguationData":[OD(0.0)],"derivedFrom":[makeQuery(id+"F1.opExtrude","SWEPT_FACE",FACE,{"disambiguationData":[OSD([subQ1])]}),makeQuery(id+"F7.opExtrude","SWEPT_FACE",FACE,{"disambiguationData":[OSD([subQ0])]})]})])],"isStart":false})})])]})]});}
            var Q9;
            {var subQ0=sQuery(id+"F0.wireOp",EDGE,"DXCdCOsZ-PZph-URoq-5IPF-RWo1TbqNF6ah");var subQ1=sQuery(id+"F6.wireOp",EDGE,"E8.left");var subQ2=sQuery(id+"F0.wireOp",EDGE,"E2");Q9=makeQuery(id+"F11.boolean.opBoolean","COPY",EDGE,{"derivedFrom":makeQuery(id+"F11.opExtrude","CAP_EDGE",EDGE,{"disambiguationData":[OSD([subQ0,subQ2]),TDD([makeQuery(id+"F8.boolean.opBoolean","SPLIT",EDGE,{"disambiguationData":[topologyDisambiguationEdgeConnected([makeQuery(id+"F5.opPattern","COPY",FACE,{"derivedFrom":makeQuery(id+"F1.opExtrude","SWEPT_FACE",FACE,{"disambiguationData":[OSD([subQ0])]}),"instanceName":"1"}),makeQuery(id+"F8.opExtrude","SWEPT_FACE",FACE,{"disambiguationData":[OSD([subQ1]),TDD([makeQuery(id+"F6.imprint","IMPRINT",EDGE,{"disambiguationData":[TD([[makeQuery(id+"F6.imprint","INTERSECT",VERTEX,{"derivedFrom":[sQuery(id+"F6.wireOp",EDGE,"E8.top"),subQ1]}),1.0]])],"derivedFrom":subQ1})])]})])],"derivedFrom":makeQuery(id+"F5.opPattern","COPY",EDGE,{"derivedFrom":makeQuery(id+"F1.opExtrude","SWEPT_EDGE",EDGE,{"disambiguationData":[OSD([subQ0,subQ2])]}),"instanceName":"1"})})])],"isStart":false})});}
            var Q10;
            {var subQ0=sQuery(id+"F6.wireOp",EDGE,"E11");var subQ1=sQuery(id+"F0.wireOp",EDGE,"E2");var subQ2=sQuery(id+"F0.wireOp",EDGE,"DXCdCOsZ-PZph-URoq-5IPF-RWo1TbqNF6ah");var subQ3=sQuery(id+"F6.wireOp",EDGE,"E8.left");Q10=makeQuery(id+"F13.boolean.opBoolean","MERGE",EDGE,{"derivedFrom":[makeQuery(id+"F11.boolean.opBoolean","COPY",EDGE,{"derivedFrom":makeQuery(id+"F11.opExtrude","CAP_EDGE",EDGE,{"disambiguationData":[OSD([subQ2,subQ1]),TDD([makeQuery(id+"F8.boolean.opBoolean","SPLIT",EDGE,{"disambiguationData":[topologyDisambiguationEdgeConnected([makeQuery(id+"F5.opPattern","COPY",FACE,{"derivedFrom":makeQuery(id+"F1.opExtrude","SWEPT_FACE",FACE,{"disambiguationData":[OSD([subQ2])]}),"instanceName":"1"}),makeQuery(id+"F8.opExtrude","SWEPT_FACE",FACE,{"disambiguationData":[OSD([subQ3]),TDD([makeQuery(id+"F6.imprint","IMPRINT",EDGE,{"disambiguationData":[TD([[makeQuery(id+"F6.imprint","INTERSECT",VERTEX,{"derivedFrom":[sQuery(id+"F6.wireOp",EDGE,"E8.bottom"),subQ3]}),-1.0]])],"derivedFrom":subQ3})])]})])],"derivedFrom":makeQuery(id+"F5.opPattern","COPY",EDGE,{"derivedFrom":makeQuery(id+"F1.opExtrude","SWEPT_EDGE",EDGE,{"disambiguationData":[OSD([subQ2,subQ1])]}),"instanceName":"1"})})])],"isStart":false})})],"fromTools":[makeQuery(id+"F13.opExtrude","SWEPT_EDGE",EDGE,{"disambiguationData":[OSD([subQ1,subQ0]),TDD([makeQuery(id+"F11.boolean.opBoolean","COPY",VERTEX,{"derivedFrom":makeQuery(id+"F11.opExtrude","CAP_VERTEX",VERTEX,{"disambiguationData":[OSD([subQ1,subQ0]),TDD([makeQuery(id+"F8.boolean.opBoolean","INTERSECT",VERTEX,{"disambiguationData":[OD(0.0)],"derivedFrom":[makeQuery(id+"F5.opPattern","COPY",FACE,{"derivedFrom":makeQuery(id+"F1.opExtrude","SWEPT_FACE",FACE,{"disambiguationData":[OSD([subQ1])]}),"instanceName":"1"}),makeQuery(id+"F8.opExtrude","SWEPT_FACE",FACE,{"disambiguationData":[OSD([subQ0])]})]})])],"isStart":false})})])]})]});}
            fillet(context, id + "F14", {"entities" : qUnion([Q0, Q1, Q2, Q3, Q4, Q5, Q6, Q7, Q8, Q9, Q10]), "radius" : 5 * mm, "tangentPropagation" : true, "allowEdgeOverflow" : false});
        }
        {
            var Q0;
            {var subQ0=sQuery(id+"F6.wireOp",EDGE,"E9");var subQ2=sQuery(id+"F0.wireOp",EDGE,"d9418fdb-b965-4b45-a9c3-fe8144ecca6f.trimOffspring");var subQ3=makeQuery(id+"F1.opExtrude","SWEPT_FACE",FACE,{"disambiguationData":[OSD([subQ2])]});var subQ4=sQuery(id+"F0.wireOp",EDGE,"E2");var subQ5=makeQuery(id+"F1.opExtrude","SWEPT_FACE",FACE,{"disambiguationData":[OSD([subQ4])]});Q0=makeQuery(id+"F7.boolean.opBoolean","SPLIT",EDGE,{"disambiguationData":[topologyDisambiguationEdgeConnected([subQ5,subQ3]),TD([makeQuery(id+"F7.opExtrude","SWEPT_FACE",FACE,{"disambiguationData":[OSD([subQ0])]})])],"derivedFrom":makeQuery(id+"F1.opExtrude","SWEPT_EDGE",EDGE,{"disambiguationData":[OSD([subQ4,subQ2])]})});}
            var Q1;
            {var subQ1=sQuery(id+"F6.wireOp",EDGE,"E9");var subQ3=sQuery(id+"F0.wireOp",EDGE,"d9418fdb-b965-4b45-a9c3-fe8144ecca6f.trimOffspring");var subQ4=makeQuery(id+"F5.opPattern","COPY",FACE,{"derivedFrom":makeQuery(id+"F1.opExtrude","SWEPT_FACE",FACE,{"disambiguationData":[OSD([subQ3])]}),"instanceName":"1"});var subQ5=sQuery(id+"F0.wireOp",EDGE,"E2");var subQ6=makeQuery(id+"F5.opPattern","COPY",FACE,{"derivedFrom":makeQuery(id+"F1.opExtrude","SWEPT_FACE",FACE,{"disambiguationData":[OSD([subQ5])]}),"instanceName":"1"});Q1=makeQuery(id+"F8.boolean.opBoolean","SPLIT",EDGE,{"disambiguationData":[topologyDisambiguationEdgeConnected([subQ6,subQ4]),TD([makeQuery(id+"F8.opExtrude","SWEPT_FACE",FACE,{"disambiguationData":[OSD([subQ1])]})])],"derivedFrom":makeQuery(id+"F5.opPattern","COPY",EDGE,{"derivedFrom":makeQuery(id+"F1.opExtrude","SWEPT_EDGE",EDGE,{"disambiguationData":[OSD([subQ5,subQ3])]}),"instanceName":"1"})});}
            var Q2;
            {var subQ2=sQuery(id+"F6.wireOp",EDGE,"E10");var subQ3=sQuery(id+"F0.wireOp",EDGE,"d9418fdb-b965-4b45-a9c3-fe8144ecca6f.trimOffspring");var subQ4=makeQuery(id+"F1.opExtrude","SWEPT_FACE",FACE,{"disambiguationData":[OSD([subQ3])]});var subQ5=sQuery(id+"F0.wireOp",EDGE,"E2");var subQ6=makeQuery(id+"F1.opExtrude","SWEPT_FACE",FACE,{"disambiguationData":[OSD([subQ5])]});Q2=makeQuery(id+"F7.boolean.opBoolean","SPLIT",EDGE,{"disambiguationData":[topologyDisambiguationEdgeConnected([subQ6,subQ4]),TD([makeQuery(id+"F7.opExtrude","SWEPT_FACE",FACE,{"disambiguationData":[OSD([subQ2])]})])],"derivedFrom":makeQuery(id+"F1.opExtrude","SWEPT_EDGE",EDGE,{"disambiguationData":[OSD([subQ5,subQ3])]})});}
            var Q3;
            {var subQ1=sQuery(id+"F6.wireOp",EDGE,"E11");var subQ2=sQuery(id+"F0.wireOp",EDGE,"d9418fdb-b965-4b45-a9c3-fe8144ecca6f.trimOffspring");var subQ3=makeQuery(id+"F1.opExtrude","SWEPT_FACE",FACE,{"disambiguationData":[OSD([subQ2])]});var subQ4=sQuery(id+"F0.wireOp",EDGE,"E2");var subQ5=makeQuery(id+"F1.opExtrude","SWEPT_FACE",FACE,{"disambiguationData":[OSD([subQ4])]});Q3=makeQuery(id+"F7.boolean.opBoolean","SPLIT",EDGE,{"disambiguationData":[topologyDisambiguationEdgeConnected([subQ5,subQ3]),TD([makeQuery(id+"F7.opExtrude","SWEPT_FACE",FACE,{"disambiguationData":[OSD([subQ1])]})])],"derivedFrom":makeQuery(id+"F1.opExtrude","SWEPT_EDGE",EDGE,{"disambiguationData":[OSD([subQ4,subQ2])]})});}
            var Q4;
            {var subQ0=sQuery(id+"F6.wireOp",EDGE,"E10");var subQ3=sQuery(id+"F0.wireOp",EDGE,"E2");var subQ4=makeQuery(id+"F5.opPattern","COPY",FACE,{"derivedFrom":makeQuery(id+"F1.opExtrude","SWEPT_FACE",FACE,{"disambiguationData":[OSD([subQ3])]}),"instanceName":"1"});var subQ5=sQuery(id+"F0.wireOp",EDGE,"DXCdCOsZ-PZph-URoq-5IPF-RWo1TbqNF6ah");var subQ6=makeQuery(id+"F5.opPattern","COPY",FACE,{"derivedFrom":makeQuery(id+"F1.opExtrude","SWEPT_FACE",FACE,{"disambiguationData":[OSD([subQ5])]}),"instanceName":"1"});Q4=makeQuery(id+"F8.boolean.opBoolean","SPLIT",EDGE,{"disambiguationData":[topologyDisambiguationEdgeConnected([subQ6,subQ4]),TD([makeQuery(id+"F8.opExtrude","SWEPT_FACE",FACE,{"disambiguationData":[OSD([subQ0])]})])],"derivedFrom":makeQuery(id+"F5.opPattern","COPY",EDGE,{"derivedFrom":makeQuery(id+"F1.opExtrude","SWEPT_EDGE",EDGE,{"disambiguationData":[OSD([subQ5,subQ3])]}),"instanceName":"1"})});}
            var Q5;
            {var subQ1=sQuery(id+"F6.wireOp",EDGE,"E9");var subQ3=sQuery(id+"F0.wireOp",EDGE,"E2");var subQ4=makeQuery(id+"F5.opPattern","COPY",FACE,{"derivedFrom":makeQuery(id+"F1.opExtrude","SWEPT_FACE",FACE,{"disambiguationData":[OSD([subQ3])]}),"instanceName":"1"});var subQ5=sQuery(id+"F0.wireOp",EDGE,"DXCdCOsZ-PZph-URoq-5IPF-RWo1TbqNF6ah");var subQ6=makeQuery(id+"F5.opPattern","COPY",FACE,{"derivedFrom":makeQuery(id+"F1.opExtrude","SWEPT_FACE",FACE,{"disambiguationData":[OSD([subQ5])]}),"instanceName":"1"});Q5=makeQuery(id+"F8.boolean.opBoolean","SPLIT",EDGE,{"disambiguationData":[topologyDisambiguationEdgeConnected([subQ6,subQ4]),TD([makeQuery(id+"F8.opExtrude","SWEPT_FACE",FACE,{"disambiguationData":[OSD([subQ1])]})])],"derivedFrom":makeQuery(id+"F5.opPattern","COPY",EDGE,{"derivedFrom":makeQuery(id+"F1.opExtrude","SWEPT_EDGE",EDGE,{"disambiguationData":[OSD([subQ5,subQ3])]}),"instanceName":"1"})});}
            fillet(context, id + "F15", {"entities" : qUnion([Q0, Q1, Q2, Q3, Q4, Q5]), "radius" : 2 * mm, "tangentPropagation" : true, "allowEdgeOverflow" : false});
        }
        {
            var Q0;
            Q0=makeQuery(id+"F7.boolean.opBoolean","INTERSECT",EDGE,{"derivedFrom":[makeQuery(id+"F1.opExtrude","SWEPT_FACE",FACE,{"disambiguationData":[OSD([sQuery(id+"F0.wireOp",EDGE,"E2")])]}),makeQuery(id+"F7.opExtrude","SWEPT_FACE",FACE,{"disambiguationData":[OSD([sQuery(id+"F6.wireOp",EDGE,"E11")])]})]});
            var Q1;
            Q1=makeQuery(id+"F7.boolean.opBoolean","INTERSECT",EDGE,{"derivedFrom":[makeQuery(id+"F1.opExtrude","SWEPT_FACE",FACE,{"disambiguationData":[OSD([sQuery(id+"F0.wireOp",EDGE,"E2")])]}),makeQuery(id+"F7.opExtrude","SWEPT_FACE",FACE,{"disambiguationData":[OSD([sQuery(id+"F6.wireOp",EDGE,"E12")])]})]});
            var Q2;
            Q2=makeQuery(id+"F1.opExtrude","CAP_EDGE",EDGE,{"disambiguationData":[OSD([sQuery(id+"F0.wireOp",EDGE,"E2")])],"isStart":false});
            var Q3;
            {var subQ0=sQuery(id+"F6.wireOp",EDGE,"E9");var subQ1=sQuery(id+"F0.wireOp",EDGE,"E2");Q3=makeQuery(id+"F12.boolean.opBoolean","COPY",EDGE,{"derivedFrom":makeQuery(id+"F12.opExtrude","CAP_EDGE",EDGE,{"disambiguationData":[OSD([subQ1,subQ0]),TDD([makeQuery(id+"F7.boolean.opBoolean","INTERSECT",EDGE,{"derivedFrom":[makeQuery(id+"F1.opExtrude","SWEPT_FACE",FACE,{"disambiguationData":[OSD([subQ1])]}),makeQuery(id+"F7.opExtrude","SWEPT_FACE",FACE,{"disambiguationData":[OSD([subQ0])]})]})])],"isStart":false})});}
            var Q4;
            {var subQ0=sQuery(id+"F6.wireOp",EDGE,"E10");var subQ1=sQuery(id+"F0.wireOp",EDGE,"E2");Q4=makeQuery(id+"F12.boolean.opBoolean","COPY",EDGE,{"derivedFrom":makeQuery(id+"F12.opExtrude","CAP_EDGE",EDGE,{"disambiguationData":[OSD([subQ1,subQ0]),TDD([makeQuery(id+"F7.boolean.opBoolean","INTERSECT",EDGE,{"derivedFrom":[makeQuery(id+"F1.opExtrude","SWEPT_FACE",FACE,{"disambiguationData":[OSD([subQ1])]}),makeQuery(id+"F7.opExtrude","SWEPT_FACE",FACE,{"disambiguationData":[OSD([subQ0])]})]})])],"isStart":false})});}
            var Q5;
            Q5=makeQuery(id+"F1.opExtrude","CAP_EDGE",EDGE,{"disambiguationData":[OSD([sQuery(id+"F0.wireOp",EDGE,"E2")])],"isStart":true});
            var Q6;
            Q6=makeQuery(id+"F7.boolean.opBoolean","INTERSECT",EDGE,{"derivedFrom":[makeQuery(id+"F3.boolean.opBoolean","COPY",FACE,{"derivedFrom":makeQuery(id+"F3.opExtrude","SWEPT_FACE",FACE,{"disambiguationData":[OSD([sQuery(id+"F2.wireOp",EDGE,"E7")])]})}),makeQuery(id+"F7.opExtrude","SWEPT_FACE",FACE,{"disambiguationData":[OSD([sQuery(id+"F6.wireOp",EDGE,"E11")])]})]});
            var Q7;
            Q7=makeQuery(id+"F12.boolean.opBoolean","COPY",EDGE,{"derivedFrom":makeQuery(id+"F12.opExtrude","CAP_EDGE",EDGE,{"disambiguationData":[OSD([sQuery(id+"F2.wireOp",EDGE,"E7"),sQuery(id+"F6.wireOp",EDGE,"E10")])],"isStart":false})});
            var Q8;
            Q8=makeQuery(id+"F7.boolean.opBoolean","INTERSECT",EDGE,{"derivedFrom":[makeQuery(id+"F3.boolean.opBoolean","COPY",FACE,{"derivedFrom":makeQuery(id+"F3.opExtrude","SWEPT_FACE",FACE,{"disambiguationData":[OSD([sQuery(id+"F2.wireOp",EDGE,"E7")])]})}),makeQuery(id+"F7.opExtrude","SWEPT_FACE",FACE,{"disambiguationData":[OSD([sQuery(id+"F6.wireOp",EDGE,"E12")])]})]});
            var Q9;
            Q9=makeQuery(id+"F12.boolean.opBoolean","COPY",EDGE,{"derivedFrom":makeQuery(id+"F12.opExtrude","CAP_EDGE",EDGE,{"disambiguationData":[OSD([sQuery(id+"F2.wireOp",EDGE,"E7"),sQuery(id+"F6.wireOp",EDGE,"E9")])],"isStart":false})});
            var Q10;
            Q10=makeQuery(id+"F3.boolean.opBoolean","INTERSECT",EDGE,{"derivedFrom":[makeQuery(id+"F1.opExtrude","CAP_FACE",FACE,{"disambiguationData":[OSD([sQuery(id+"F0.wireOp",EDGE,"DXCdCOsZ-PZph-URoq-5IPF-RWo1TbqNF6ah"),sQuery(id+"F0.wireOp",EDGE,"ewKAHVJC-rmJ0-RbaL-eWMY-Gv7xBNoriCzo"),sQuery(id+"F0.wireOp",EDGE,"E2"),sQuery(id+"F0.wireOp",EDGE,"d9418fdb-b965-4b45-a9c3-fe8144ecca6f.trimOffspring")])],"isStart":false}),makeQuery(id+"F3.opExtrude","SWEPT_FACE",FACE,{"disambiguationData":[OSD([sQuery(id+"F2.wireOp",EDGE,"E7")])]})]});
            fillet(context, id + "F16", {"entities" : qUnion([Q0, Q1, Q2, Q3, Q4, Q5, Q6, Q7, Q8, Q9, Q10]), "radius" : 2 * mm, "tangentPropagation" : true, "allowEdgeOverflow" : false});
        }
        {
            var Q0;
            Q0=makeQuery(id+"F8.boolean.opBoolean","INTERSECT",EDGE,{"derivedFrom":[makeQuery(id+"F5.opPattern","COPY",FACE,{"derivedFrom":makeQuery(id+"F3.boolean.opBoolean","COPY",FACE,{"derivedFrom":makeQuery(id+"F3.opExtrude","SWEPT_FACE",FACE,{"disambiguationData":[OSD([sQuery(id+"F2.wireOp",EDGE,"E7")])]})}),"instanceName":"1"}),makeQuery(id+"F8.opExtrude","SWEPT_FACE",FACE,{"disambiguationData":[OSD([sQuery(id+"F6.wireOp",EDGE,"E9")])]})]});
            var Q1;
            Q1=makeQuery(id+"F8.boolean.opBoolean","INTERSECT",EDGE,{"derivedFrom":[makeQuery(id+"F5.opPattern","COPY",FACE,{"derivedFrom":makeQuery(id+"F1.opExtrude","SWEPT_FACE",FACE,{"disambiguationData":[OSD([sQuery(id+"F0.wireOp",EDGE,"E2")])]}),"instanceName":"1"}),makeQuery(id+"F8.opExtrude","SWEPT_FACE",FACE,{"disambiguationData":[OSD([sQuery(id+"F6.wireOp",EDGE,"E9")])]})]});
            var Q2;
            {var subQ0=sQuery(id+"F0.wireOp",EDGE,"E2");var subQ1=makeQuery(id+"F1.opExtrude","SWEPT_FACE",FACE,{"disambiguationData":[OSD([subQ0])]});var subQ2=makeQuery(id+"F5.opPattern","COPY",FACE,{"derivedFrom":subQ1,"instanceName":"1"});var subQ3=sQuery(id+"F6.wireOp",EDGE,"E12");var subQ4=makeQuery(id+"F8.opExtrude","SWEPT_FACE",FACE,{"disambiguationData":[OSD([subQ3])]});var subQ6=makeQuery(id+"F7.opExtrude","SWEPT_FACE",FACE,{"disambiguationData":[OSD([subQ3])]});var subQ8=makeQuery(id+"F8.boolean.opBoolean","INTERSECT",EDGE,{"derivedFrom":[subQ2,subQ4]});var subQ9=makeQuery(id+"F12.opExtrude","CAP_FACE",FACE,{"disambiguationData":[OSD([sQuery(id+"F6.wireOp",EDGE,"E8.right"),subQ3])],"isStart":false});var subQ11=sQuery(id+"F6.wireOp",EDGE,"E9");var subQ12=makeQuery(id+"F8.boolean.opBoolean","SPLIT",FACE,{"disambiguationData":[TD([makeQuery(id+"F8.opExtrude","SWEPT_FACE",FACE,{"disambiguationData":[OSD([subQ11])]})])],"derivedFrom":subQ2});Q2=makeQuery(id+"F13.boolean.opBoolean","MERGE",EDGE,{"derivedFrom":[makeQuery(id+"F12.boolean.opBoolean","INTERSECT",EDGE,{"disambiguationData":[OD(0.0)],"derivedFrom":[subQ12,subQ9]}),makeQuery(id+"F12.boolean.opBoolean","INTERSECT",EDGE,{"disambiguationData":[OD(1.0)],"derivedFrom":[subQ12,subQ9]}),makeQuery(id+"F12.boolean.opBoolean","INTERSECT",EDGE,{"disambiguationData":[OD(2.0)],"derivedFrom":[subQ12,subQ9]})],"fromTools":[makeQuery(id+"F13.opExtrude","CAP_EDGE",EDGE,{"disambiguationData":[OSD([subQ0,subQ3]),TDD([makeQuery(id+"F12.boolean.opBoolean","SPLIT",EDGE,{"disambiguationData":[TD([makeQuery(id+"F12.opExtrude","SWEPT_FACE",FACE,{"disambiguationData":[OSD([subQ0,subQ3]),TDD([makeQuery(id+"F10.boolean.opBoolean","COPY",EDGE,{"derivedFrom":makeQuery(id+"F10.opExtrude","SWEPT_EDGE",EDGE,{"disambiguationData":[OSD([subQ0,subQ3]),TDD([makeQuery(id+"F7.boolean.opBoolean","INTERSECT",VERTEX,{"disambiguationData":[OD(0.0)],"derivedFrom":[subQ1,subQ6]})])]})})])]})])],"derivedFrom":subQ8})])],"isStart":false}),makeQuery(id+"F13.opExtrude","CAP_EDGE",EDGE,{"disambiguationData":[OSD([subQ0,subQ3]),TDD([makeQuery(id+"F12.boolean.opBoolean","SPLIT",EDGE,{"disambiguationData":[TD([makeQuery(id+"F12.opExtrude","SWEPT_FACE",FACE,{"disambiguationData":[OSD([subQ0,subQ3]),TDD([makeQuery(id+"F10.boolean.opBoolean","COPY",EDGE,{"derivedFrom":makeQuery(id+"F10.opExtrude","SWEPT_EDGE",EDGE,{"disambiguationData":[OSD([subQ0,subQ3]),TDD([makeQuery(id+"F7.boolean.opBoolean","INTERSECT",VERTEX,{"disambiguationData":[OD(1.0)],"derivedFrom":[subQ1,subQ6]})])]})})])]})])],"derivedFrom":subQ8})])],"isStart":false})]});}
            var Q3;
            {var subQ0=sQuery(id+"F6.wireOp",EDGE,"E12");var subQ1=makeQuery(id+"F8.opExtrude","SWEPT_FACE",FACE,{"disambiguationData":[OSD([subQ0])]});var subQ2=sQuery(id+"F2.wireOp",EDGE,"E7");var subQ3=makeQuery(id+"F5.opPattern","COPY",FACE,{"derivedFrom":makeQuery(id+"F3.boolean.opBoolean","COPY",FACE,{"derivedFrom":makeQuery(id+"F3.opExtrude","SWEPT_FACE",FACE,{"disambiguationData":[OSD([subQ2])]})}),"instanceName":"1"});Q3=makeQuery(id+"F13.boolean.opBoolean","MERGE",EDGE,{"derivedFrom":[makeQuery(id+"F12.boolean.opBoolean","INTERSECT",EDGE,{"derivedFrom":[makeQuery(id+"F8.boolean.opBoolean","SPLIT",FACE,{"disambiguationData":[TD([makeQuery(id+"F8.opExtrude","SWEPT_FACE",FACE,{"disambiguationData":[OSD([sQuery(id+"F6.wireOp",EDGE,"E9")])]})])],"derivedFrom":subQ3}),makeQuery(id+"F12.opExtrude","CAP_FACE",FACE,{"disambiguationData":[OSD([sQuery(id+"F6.wireOp",EDGE,"E8.right"),subQ0])],"isStart":false})]})],"fromTools":[makeQuery(id+"F13.opExtrude","CAP_EDGE",EDGE,{"disambiguationData":[OSD([subQ2,subQ0]),TDD([makeQuery(id+"F8.boolean.opBoolean","INTERSECT",EDGE,{"derivedFrom":[subQ3,subQ1]})])],"isStart":false})]});}
            var Q4;
            {var subQ0=sQuery(id+"F6.wireOp",EDGE,"E11");var subQ1=makeQuery(id+"F8.opExtrude","SWEPT_FACE",FACE,{"disambiguationData":[OSD([subQ0])]});var subQ2=sQuery(id+"F2.wireOp",EDGE,"E7");var subQ3=makeQuery(id+"F5.opPattern","COPY",FACE,{"derivedFrom":makeQuery(id+"F3.boolean.opBoolean","COPY",FACE,{"derivedFrom":makeQuery(id+"F3.opExtrude","SWEPT_FACE",FACE,{"disambiguationData":[OSD([subQ2])]})}),"instanceName":"1"});Q4=makeQuery(id+"F13.boolean.opBoolean","MERGE",EDGE,{"derivedFrom":[makeQuery(id+"F12.boolean.opBoolean","INTERSECT",EDGE,{"derivedFrom":[makeQuery(id+"F8.boolean.opBoolean","SPLIT",FACE,{"disambiguationData":[TD([makeQuery(id+"F8.opExtrude","SWEPT_FACE",FACE,{"disambiguationData":[OSD([sQuery(id+"F6.wireOp",EDGE,"E10")])]})])],"derivedFrom":subQ3}),makeQuery(id+"F12.opExtrude","CAP_FACE",FACE,{"disambiguationData":[OSD([sQuery(id+"F6.wireOp",EDGE,"E8.right"),subQ0])],"isStart":false})]})],"fromTools":[makeQuery(id+"F13.opExtrude","CAP_EDGE",EDGE,{"disambiguationData":[OSD([subQ2,subQ0]),TDD([makeQuery(id+"F8.boolean.opBoolean","INTERSECT",EDGE,{"derivedFrom":[subQ3,subQ1]})])],"isStart":false})]});}
            var Q5;
            {var subQ0=sQuery(id+"F0.wireOp",EDGE,"E2");var subQ1=makeQuery(id+"F1.opExtrude","SWEPT_FACE",FACE,{"disambiguationData":[OSD([subQ0])]});var subQ2=makeQuery(id+"F5.opPattern","COPY",FACE,{"derivedFrom":subQ1,"instanceName":"1"});var subQ3=sQuery(id+"F6.wireOp",EDGE,"E11");var subQ4=makeQuery(id+"F8.opExtrude","SWEPT_FACE",FACE,{"disambiguationData":[OSD([subQ3])]});var subQ6=makeQuery(id+"F7.opExtrude","SWEPT_FACE",FACE,{"disambiguationData":[OSD([subQ3])]});var subQ8=makeQuery(id+"F8.boolean.opBoolean","INTERSECT",EDGE,{"derivedFrom":[subQ2,subQ4]});var subQ9=makeQuery(id+"F12.opExtrude","CAP_FACE",FACE,{"disambiguationData":[OSD([sQuery(id+"F6.wireOp",EDGE,"E8.right"),subQ3])],"isStart":false});var subQ11=sQuery(id+"F6.wireOp",EDGE,"E10");var subQ12=makeQuery(id+"F8.boolean.opBoolean","SPLIT",FACE,{"disambiguationData":[TD([makeQuery(id+"F8.opExtrude","SWEPT_FACE",FACE,{"disambiguationData":[OSD([subQ11])]})])],"derivedFrom":subQ2});Q5=makeQuery(id+"F13.boolean.opBoolean","MERGE",EDGE,{"derivedFrom":[makeQuery(id+"F12.boolean.opBoolean","INTERSECT",EDGE,{"disambiguationData":[OD(0.0)],"derivedFrom":[subQ12,subQ9]}),makeQuery(id+"F12.boolean.opBoolean","INTERSECT",EDGE,{"disambiguationData":[OD(1.0)],"derivedFrom":[subQ12,subQ9]}),makeQuery(id+"F12.boolean.opBoolean","INTERSECT",EDGE,{"disambiguationData":[OD(2.0)],"derivedFrom":[subQ12,subQ9]})],"fromTools":[makeQuery(id+"F13.opExtrude","CAP_EDGE",EDGE,{"disambiguationData":[OSD([subQ0,subQ3]),TDD([makeQuery(id+"F12.boolean.opBoolean","SPLIT",EDGE,{"disambiguationData":[TD([makeQuery(id+"F12.opExtrude","SWEPT_FACE",FACE,{"disambiguationData":[OSD([subQ0,subQ3]),TDD([makeQuery(id+"F10.boolean.opBoolean","COPY",EDGE,{"derivedFrom":makeQuery(id+"F10.opExtrude","SWEPT_EDGE",EDGE,{"disambiguationData":[OSD([subQ0,subQ3]),TDD([makeQuery(id+"F7.boolean.opBoolean","INTERSECT",VERTEX,{"disambiguationData":[OD(0.0)],"derivedFrom":[subQ1,subQ6]})])]})})])]})])],"derivedFrom":subQ8})])],"isStart":false}),makeQuery(id+"F13.opExtrude","CAP_EDGE",EDGE,{"disambiguationData":[OSD([subQ0,subQ3]),TDD([makeQuery(id+"F12.boolean.opBoolean","SPLIT",EDGE,{"disambiguationData":[TD([makeQuery(id+"F12.opExtrude","SWEPT_FACE",FACE,{"disambiguationData":[OSD([subQ0,subQ3]),TDD([makeQuery(id+"F10.boolean.opBoolean","COPY",EDGE,{"derivedFrom":makeQuery(id+"F10.opExtrude","SWEPT_EDGE",EDGE,{"disambiguationData":[OSD([subQ0,subQ3]),TDD([makeQuery(id+"F7.boolean.opBoolean","INTERSECT",VERTEX,{"disambiguationData":[OD(1.0)],"derivedFrom":[subQ1,subQ6]})])]})})])]})])],"derivedFrom":subQ8})])],"isStart":false})]});}
            var Q6;
            Q6=makeQuery(id+"F8.boolean.opBoolean","INTERSECT",EDGE,{"derivedFrom":[makeQuery(id+"F5.opPattern","COPY",FACE,{"derivedFrom":makeQuery(id+"F3.boolean.opBoolean","COPY",FACE,{"derivedFrom":makeQuery(id+"F3.opExtrude","SWEPT_FACE",FACE,{"disambiguationData":[OSD([sQuery(id+"F2.wireOp",EDGE,"E7")])]})}),"instanceName":"1"}),makeQuery(id+"F8.opExtrude","SWEPT_FACE",FACE,{"disambiguationData":[OSD([sQuery(id+"F6.wireOp",EDGE,"E10")])]})]});
            var Q7;
            Q7=makeQuery(id+"F8.boolean.opBoolean","INTERSECT",EDGE,{"derivedFrom":[makeQuery(id+"F5.opPattern","COPY",FACE,{"derivedFrom":makeQuery(id+"F1.opExtrude","SWEPT_FACE",FACE,{"disambiguationData":[OSD([sQuery(id+"F0.wireOp",EDGE,"E2")])]}),"instanceName":"1"}),makeQuery(id+"F8.opExtrude","SWEPT_FACE",FACE,{"disambiguationData":[OSD([sQuery(id+"F6.wireOp",EDGE,"E10")])]})]});
            var Q8;
            Q8=makeQuery(id+"F5.opPattern","COPY",EDGE,{"derivedFrom":makeQuery(id+"F1.opExtrude","CAP_EDGE",EDGE,{"disambiguationData":[OSD([sQuery(id+"F0.wireOp",EDGE,"DXCdCOsZ-PZph-URoq-5IPF-RWo1TbqNF6ah")])],"isStart":false}),"instanceName":"1"});
            var Q9;
            Q9=makeQuery(id+"F5.opPattern","COPY",EDGE,{"derivedFrom":makeQuery(id+"F1.opExtrude","CAP_EDGE",EDGE,{"disambiguationData":[OSD([sQuery(id+"F0.wireOp",EDGE,"DXCdCOsZ-PZph-URoq-5IPF-RWo1TbqNF6ah")])],"isStart":true}),"instanceName":"1"});
            fillet(context, id + "F17", {"entities" : qUnion([Q0, Q1, Q2, Q3, Q4, Q5, Q6, Q7, Q8, Q9]), "radius" : 2 * mm, "tangentPropagation" : true, "allowEdgeOverflow" : false});
        }
    });
